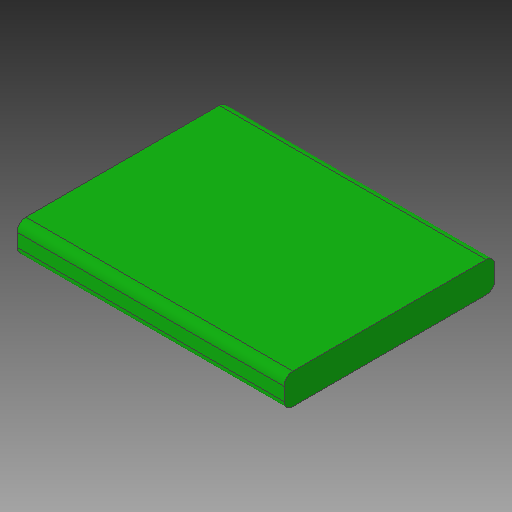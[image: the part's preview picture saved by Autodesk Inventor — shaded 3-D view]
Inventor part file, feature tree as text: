
AUTODESK INVENTOR PART (.ipt)
format: ipt  version: 2018 (Build 220112000, 112)  size: 105,472 bytes
history: native  units: mm
features: extrude x1, fillet x1, sketch x1
ambient origin geometry x8: Origin, YZ Plane, XZ Plane, XY Plane, X Axis, Y Axis, Z Axis, Center Point
bodies: Solid1 (feature_tree)
feature tree (3):
  extrude  "Extrusion1"  Depth=60.96mm
  fillet  "Fillet1"  Radius=7.0mm
  sketch  "Sketch1"  dims[d0=48.15mm d1=60.96mm d2=7.0mm d3=0.0mm d4=2.0mm]
